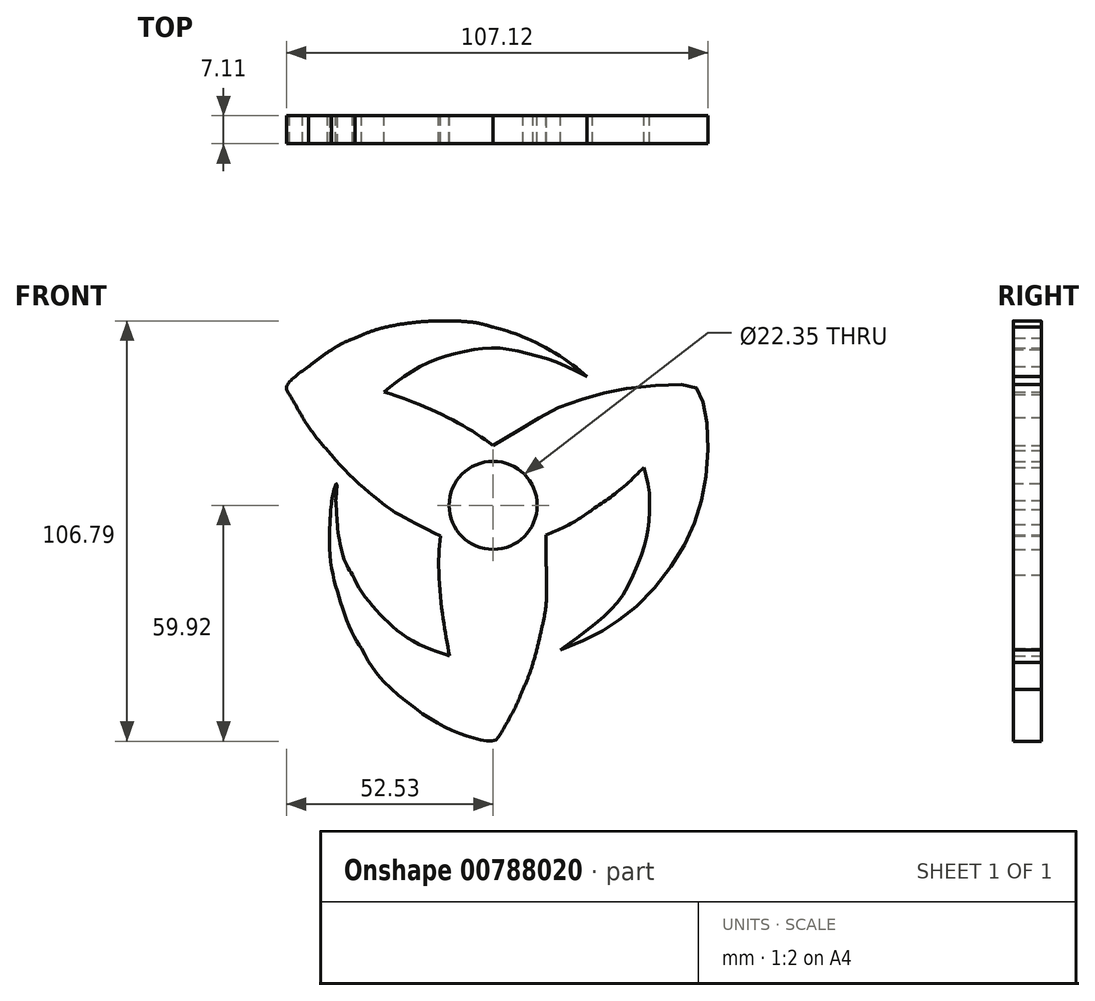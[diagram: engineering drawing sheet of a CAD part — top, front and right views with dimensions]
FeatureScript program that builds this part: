
annotation { "Feature Type Name" : "Feature", "Feature Type Description" : "" }
export const myFeature = defineFeature(function(context is Context, id is Id, definition is map)
    precondition{}
    {
        {
            var Q0;
            Q0=qCreatedBy(makeId("Front.planeOp"),FACE);
            var sketch = newSketch(context, id + "F0", { "sketchPlane" : qUnion([Q0])});
            skFitSpline(sketch, "E0", {"points": [v(-33.4, -36.4) * mm, v(-35.63, -32.78) * mm, v(-38.08, -26.67) * mm, v(-39.87, -20.97) * mm, v(-41.27, -14.53) * mm, v(-41.6, -7.76) * mm, v(-41.46, -4.85) * mm], "startDerivative": vector(-15.3, 22.36) * mm, "endDerivative": vector(1.4, 21.12) * mm});
            skFitSpline(sketch, "E1", {"points": [v(-13.37, -7.78) * mm, v(-13.85, -14.64) * mm, v(-13.21, -24.9) * mm, v(-12.19, -32.24) * mm, v(-11.1, -38.23) * mm], "startDerivative": vector(-2.88, -26.93) * mm, "endDerivative": vector(5.03, -26.47) * mm});
            skFitSpline(sketch, "E2", {"points": [v(-11.1, -38.23) * mm, v(-14.72, -37) * mm, v(-21.25, -34) * mm, v(-26.5, -29.92) * mm, v(-30.4, -25.85) * mm, v(-33.85, -21.33) * mm, v(-35.75, -17.64) * mm], "startDerivative": vector(-23.84, 7.58) * mm, "endDerivative": vector(-11.38, 24.9) * mm});
            skFitSpline(sketch, "E3", {"points": [v(-35.75, -17.64) * mm, v(-37.48, -14.6) * mm, v(-39.2, -8.16) * mm, v(-39.74, -2.52) * mm, v(-40, 1.26) * mm], "startDerivative": vector(-8.4, 12.54) * mm, "endDerivative": vector(-1.22, 16.35) * mm});
            skFitSpline(sketch, "E4", {"points": [v(-41.46, -4.85) * mm, v(-40.87, 1.99) * mm, v(-39.8, 5.44) * mm, v(-40, 1.26) * mm], "startDerivative": vector(0.52, 16.86) * mm, "endDerivative": vector(-1.94, -20.03) * mm});
            skFitSpline(sketch, "E5", {"points": [v(-13.37, -7.78) * mm, v(-21.3, -3.77) * mm, v(-26.18, -0.93) * mm, v(-30.52, 2.46) * mm, v(-36.83, 8.07) * mm, v(-42.12, 13.98) * mm], "startDerivative": vector(-37.75, 18.82) * mm, "endDerivative": vector(-23.78, 28.4) * mm});
            skFitSpline(sketch, "E6", {"points": [v(-42.12, 13.98) * mm, v(-44.98, 17.31) * mm, v(-48.43, 22.35) * mm, v(-51.55, 27.8) * mm, v(-52.46, 30.21) * mm, v(-46.11, 35.86) * mm, v(-39.58, 40.44) * mm, v(-35.12, 42.5) * mm, v(-29.5, 44.69) * mm, v(-20.86, 46.36) * mm, v(-13.37, 46.87) * mm, v(-4.62, 46.42) * mm, v(0, 45.25) * mm], "startDerivative": vector(-40.46, 44.98) * mm, "endDerivative": vector(56.97, -18.23) * mm});
            skFitSpline(sketch, "E7", {"points": [v(0, 45.25) * mm, v(4.26, 44.03) * mm, v(9.9, 41.77) * mm, v(18.06, 37.2) * mm, v(23.84, 32.75) * mm], "startDerivative": vector(20.56, -5.48) * mm, "endDerivative": vector(20.46, -17.02) * mm});
            skFitSpline(sketch, "E8", {"points": [v(-27.78, 28.83) * mm, v(-23.6, 32.02) * mm, v(-17.76, 35.67) * mm, v(-11.46, 38.05) * mm, v(-4.62, 39.58) * mm, v(1.15, 39.98) * mm, v(7.58, 38.85) * mm, v(15.14, 36.73) * mm, v(23.84, 32.75) * mm], "startDerivative": vector(36.4, 28.62) * mm, "endDerivative": vector(59.52, -29.9) * mm});
            skPoint(sketch, "E9.5.internal.orphan", {"position": v(0, 15.45) * mm});
            skFitSpline(sketch, "E10", {"points": [v(0, 15.25) * mm, v(-5.99, 19.26) * mm, v(-14.4, 23.7) * mm, v(-23.23, 27.34) * mm, v(-27.78, 28.83) * mm], "startDerivative": vector(-23.53, 16.59) * mm, "endDerivative": vector(-21.04, 6.5) * mm});
            skFitSpline(sketch, "E11", {"points": [v(38.34, 9.67) * mm, v(39.67, 2.9) * mm, v(39.4, -5) * mm, v(38.08, -11.36) * mm, v(33.65, -21.63) * mm, v(28.13, -28.25) * mm, v(19.6, -34.88) * mm, v(17.12, -36.76) * mm], "startDerivative": vector(12.42, -47.92) * mm, "endDerivative": vector(-22.18, -16.96) * mm});
            skFitSpline(sketch, "E12", {"points": [v(13.46, -7.57) * mm, v(20.36, -4.32) * mm, v(25.2, -1.06) * mm], "startDerivative": vector(13.61, 5.86) * mm, "endDerivative": vector(9.79, 7.17) * mm});
            skFitSpline(sketch, "E13", {"points": [v(25.2, -1.06) * mm, v(29.25, 1.66) * mm, v(33.7, 5.24) * mm, v(38.34, 9.67) * mm], "startDerivative": vector(13, 8.4) * mm, "endDerivative": vector(13, 12.83) * mm});
            skPoint(sketch, "E14.5.internal.orphan", {"position": v(52.5, 0) * mm});
            skPoint(sketch, "E15.end.orphan", {"position": v(52.5, 30.13) * mm});
            skFitSpline(sketch, "E16.trimOffspring", {"points": [v(13.46, -7.57) * mm, v(13.46, -15.32) * mm, v(13.46, -24.86) * mm, v(12.16, -31.96) * mm, v(10.17, -39.91) * mm, v(7.54, -46.78) * mm, v(2.08, -57.66) * mm, v(0, -60.54) * mm, v(-3.12, -60.25) * mm], "startDerivative": vector(-0.68, -56.77) * mm, "endDerivative": vector(-41.74, 10.78) * mm});
            skFitSpline(sketch, "E17", {"points": [v(-42.12, 13.98) * mm, v(-45.37, 18.16) * mm, v(-48.43, 22.35) * mm, v(-50.86, 26.62) * mm, v(-52.22, 29.24) * mm, v(-51.13, 31.6) * mm, v(-39.58, 40.44) * mm, v(-35.12, 42.5) * mm, v(-29.5, 44.69) * mm, v(-20.86, 46.36) * mm, v(-13.37, 46.87) * mm, v(-4.62, 46.42) * mm, v(0, 45.25) * mm], "startDerivative": vector(-41.67, 53.7) * mm, "endDerivative": vector(56.08, -17.93) * mm});
            skFitSpline(sketch, "E18", {"points": [v(-33.4, -36.4) * mm, v(-29.5, -42.84) * mm, v(-19.37, -51.9) * mm, v(-10.95, -56.93) * mm, v(-3.64, -59.46) * mm, v(0.35, -59.74) * mm, v(2.08, -57.66) * mm, v(5.44, -51.65) * mm, v(7.54, -46.78) * mm, v(10.17, -39.91) * mm, v(12.16, -31.96) * mm, v(13.46, -24.86) * mm, v(13.46, -15.32) * mm, v(13.46, -7.57) * mm], "startDerivative": vector(38.75, -79.76) * mm, "endDerivative": vector(1.16, 93.57) * mm});
            skPoint(sketch, "E19.2.internal.orphan", {"position": v(10.17, 21.25) * mm});
            skFitSpline(sketch, "E20", {"points": [v(0, 15.25) * mm, v(10.17, 21.25) * mm, v(17.05, 24.98) * mm, v(25.91, 27.85) * mm, v(33.93, 29.7) * mm, v(46.46, 30.63) * mm, v(51.28, 30.13) * mm, v(52.98, 27.47) * mm, v(54.29, 20.8) * mm, v(54.36, 9.46) * mm, v(52.5, 0) * mm, v(49.44, -8.41) * mm, v(44.03, -17.13) * mm, v(36.77, -25.4) * mm, v(30.78, -29.96) * mm, v(25.55, -33.17) * mm, v(17.12, -36.76) * mm], "startDerivative": vector(146.35, 85.7) * mm, "endDerivative": vector(-138.85, -54.24) * mm});
            skCircle(sketch, "E21", {"center": v(0, 0) * mm, "radius": 11.18 * mm});
            skSolve(sketch);
        }
        {
            var Q0;
            Q0 = qSketchRegion(id + "F0", true);
            extrude(context, id + "F1", {"entities" : qUnion([Q0]), "depth" : 7 * mm, "offsetDistance" : 25.4 * mm});
        }
        {
            var Q0;
            Q0 = qSketchRegion(id + "F0", true);
            extrude(context, id + "F2", {"entities" : qUnion([Q0]), "operationType" : NewBodyOperationType.ADD, "depth" : 7.11 * mm, "offsetDistance" : 25.4 * mm});
        }
    });
